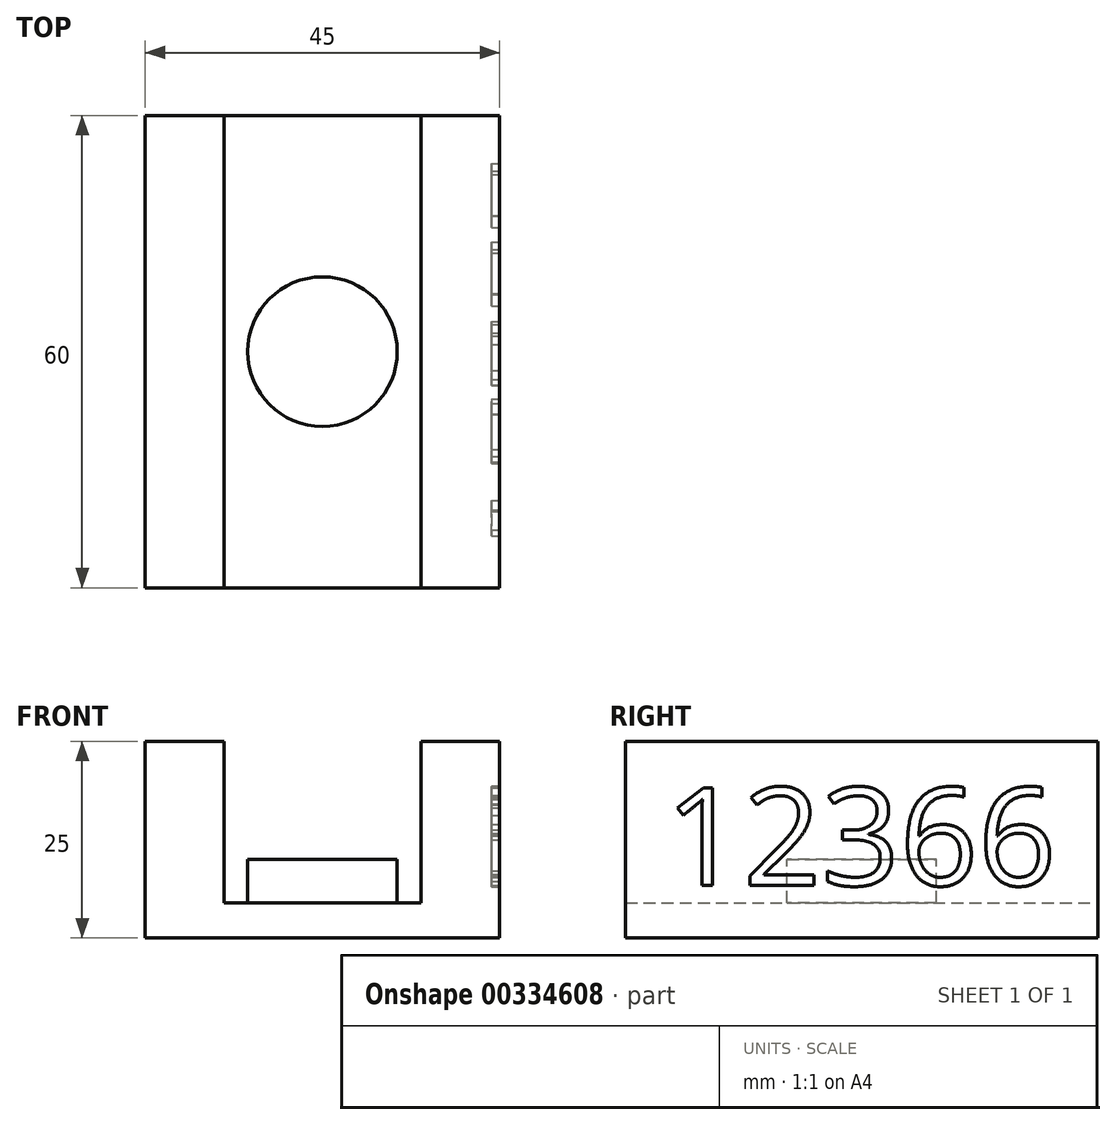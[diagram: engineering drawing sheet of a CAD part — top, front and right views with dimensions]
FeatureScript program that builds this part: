
annotation { "Feature Type Name" : "Feature", "Feature Type Description" : "" }
export const myFeature = defineFeature(function(context is Context, id is Id, definition is map)
    precondition{}
    {
        {
            var Q0;
            Q0=qCreatedBy(makeId("Front.planeOp"),FACE);
            var sketch = newSketch(context, id + "F0", { "sketchPlane" : qUnion([Q0])});
            skLineSegment(sketch, "E0.bottom", {"start": v(22.5, -12.5) * mm, "end": v(-22.5, -12.5) * mm});
            skLineSegment(sketch, "E0.top", {"start": v(22.5, 12.5) * mm, "end": v(-22.5, 12.5) * mm});
            skLineSegment(sketch, "E0.left", {"start": v(22.5, -12.5) * mm, "end": v(22.5, 12.5) * mm});
            skLineSegment(sketch, "E0.right", {"start": v(-22.5, -12.5) * mm, "end": v(-22.5, 12.5) * mm});
            skPoint(sketch, "E0.middle", {"position": v(0, 0) * mm});
            skLineSegment(sketch, "E1.bottom", {"start": v(12.5, -2.5) * mm, "end": v(-12.5, -2.5) * mm});
            skLineSegment(sketch, "E1.top", {"start": v(12.5, 27.5) * mm, "end": v(-12.5, 27.5) * mm});
            skLineSegment(sketch, "E1.left", {"start": v(12.5, -2.5) * mm, "end": v(12.5, 27.5) * mm});
            skLineSegment(sketch, "E1.right", {"start": v(-12.5, -2.5) * mm, "end": v(-12.5, 27.5) * mm});
            skPoint(sketch, "E1.middle", {"position": v(0, 12.5) * mm});
            skSolve(sketch);
        }
        {
            var Q0;
            Q0=makeQuery(id+"F0.imprint","IMPRINT",FACE,{"disambiguationData":[TD([[makeQuery(id+"F0.imprint","IMPRINT",EDGE,{"derivedFrom":sQuery(id+"F0.wireOp",EDGE,"E0.bottom")}),-1.0]])]});
            extrude(context, id + "F1", {"entities" : qUnion([Q0]), "depth" : 60 * mm});
        }
        {
            var Q0;
            Q0=makeQuery(id+"F1.opExtrude","SWEPT_FACE",FACE,{"disambiguationData":[OSD([sQuery(id+"F0.wireOp",EDGE,"E0.left")])]});
            var sketch = newSketch(context, id + "F2", { "sketchPlane" : qUnion([Q0])});
            skText(sketch, "E2", { "text": "12366", "fontName": "OpenSans-Regular.ttf"});
            const initialGuessF2  = {"E2": [-0.055, -0.00581, 1, 0, 0.01252]};
            skSetInitialGuess(sketch, initialGuessF2);
            skSolve(sketch);
        }
        {
            var Q0;
            Q0 = qSketchRegion(id + "F2", true);
            extrude(context, id + "F3", {"entities" : qUnion([Q0]), "operationType" : NewBodyOperationType.REMOVE, "oppositeDirection" : true, "depth" : 1 * mm});
        }
        {
            var Q0;
            Q0=makeQuery(id+"F1.opExtrude","SWEPT_FACE",FACE,{"disambiguationData":[OSD([sQuery(id+"F0.wireOp",EDGE,"E1.bottom")])]});
            var sketch = newSketch(context, id + "F4", { "sketchPlane" : qUnion([Q0])});
            skLineSegment(sketch, "E3", {"start": v(0, 0) * mm, "end": v(0, -60) * mm});
            skPoint(sketch, "E4", {"position": v(0, -30) * mm});
            skCircle(sketch, "E5", {"center": v(0, -30) * mm, "radius": 9.5 * mm});
            skSolve(sketch);
        }
        {
            var Q0;
            {var subQ0=sQuery(id+"F4.wireOp",EDGE,"E5");var subQ1=sQuery(id+"F4.wireOp",EDGE,"E3");var subQ2=makeQuery(id+"F4.imprint","INTERSECT",VERTEX,{"disambiguationData":[OD(0.0)],"derivedFrom":[subQ1,subQ0]});Q0=makeQuery(id+"F4.imprint","IMPRINT",FACE,{"disambiguationData":[TD([[makeQuery(id+"F4.imprint","IMPRINT",EDGE,{"disambiguationData":[TD([[subQ2,-1.0]])],"derivedFrom":subQ1}),-1.0]])]});}
            var Q1;
            {var subQ0=sQuery(id+"F4.wireOp",EDGE,"E5");var subQ1=sQuery(id+"F4.wireOp",EDGE,"E3");var subQ2=makeQuery(id+"F4.imprint","INTERSECT",VERTEX,{"disambiguationData":[OD(0.0)],"derivedFrom":[subQ1,subQ0]});Q1=makeQuery(id+"F4.imprint","IMPRINT",FACE,{"disambiguationData":[TD([[makeQuery(id+"F4.imprint","IMPRINT",EDGE,{"disambiguationData":[TD([[subQ2,-1.0]])],"derivedFrom":subQ1}),1.0]])]});}
            extrude(context, id + "F5", {"entities" : qUnion([Q0, Q1]), "operationType" : NewBodyOperationType.REMOVE, "oppositeDirection" : true, "depth" : 5.5 * mm});
        }
    });
